# Revit family: R 10 V.V.
name_source: partatom
category: Equipement spécialisé
revit_build: Autodesk Revit LT 2014 (Build: 20130308_1515(x64)
units: mm (PartAtom-declared; Revit-internal decimal feet)

## types (1)
- R 10 V.V.   230/50/1
    Amps = 21 A
    Apparent Power = 0 VA
    Cold water supply = 0 mm  [stored 0 ft]
    Cold water supply height = 0 mm  [stored 0 ft]
    Cycle = 50 Hz
    Depth = 595 mm
    Description = CUTTERS DE TABLE
    Electrique connexion = 100 mm  [stored 0.328084 ft]
    Fabricant = ROBOT COUPE
    Height = 660 mm
    Modèle = R 10 V.V.
    Phase = 1
    Speeds (Rpm) = 300 to 3500
    URL = www.robot-coupe.com
    Used water = 0 mm  [stored 0 ft]
    Volts = 230 V
    Waste water height = 0 mm  [stored 0 ft]
    Watts = 2600 W
    Weight = 50.6 kg
    Width = 372 mm
    water = Connector

note: [stored X ft] marks values corroborated as IEEE doubles in the binary element streams (Revit-internal decimal feet)

## geometry (parser evidence)
native form markers: Blend x104, Sweep x3
no freeform markers — native parametric forms only
